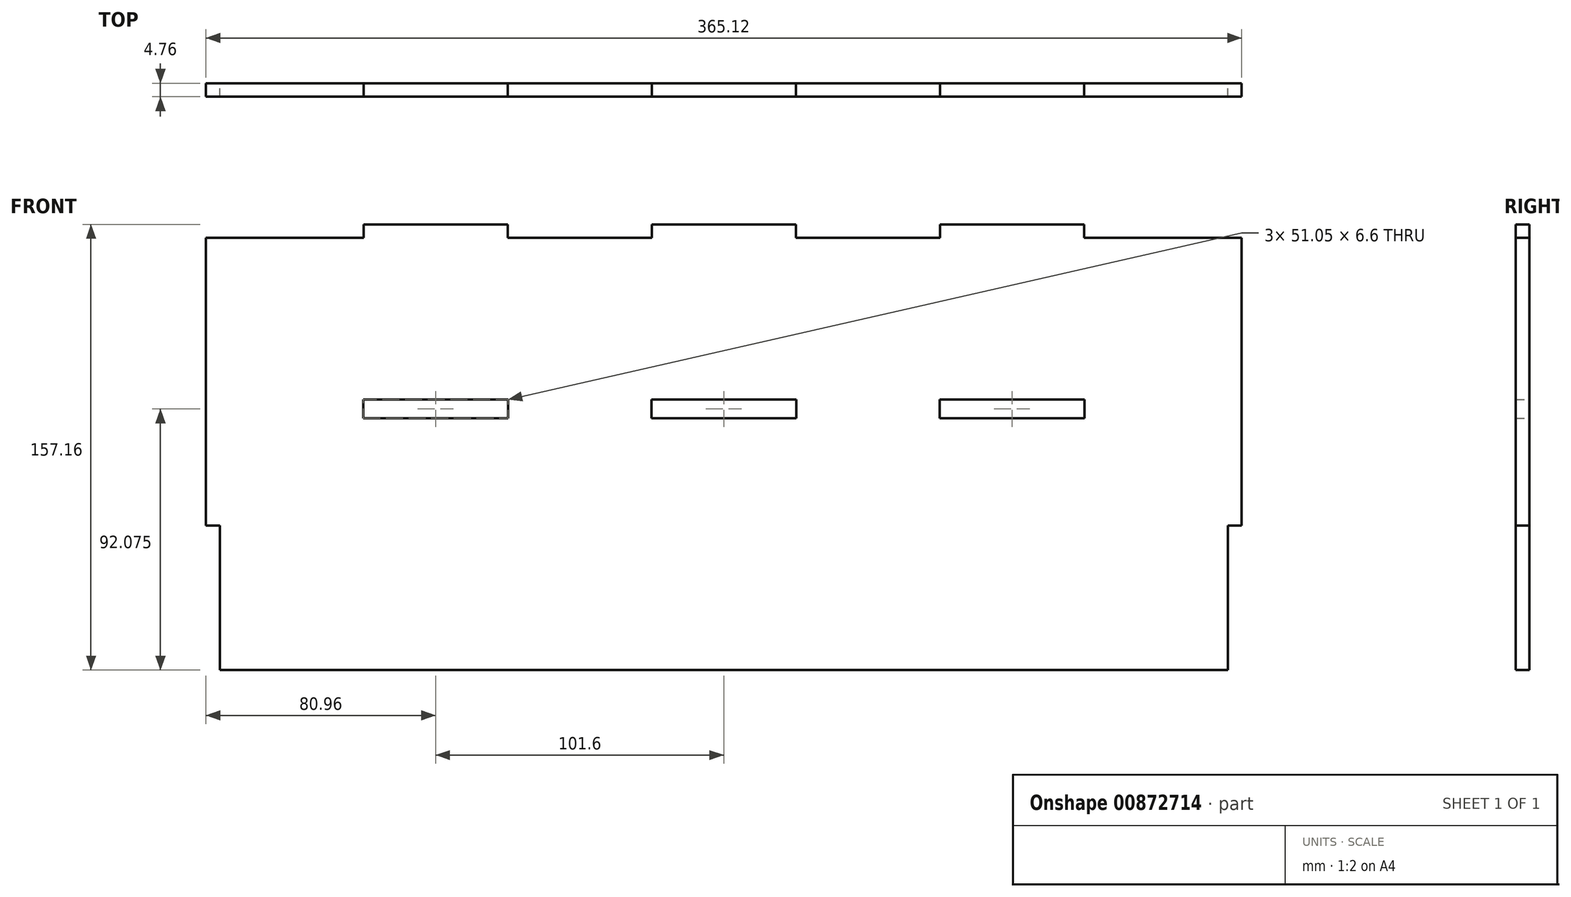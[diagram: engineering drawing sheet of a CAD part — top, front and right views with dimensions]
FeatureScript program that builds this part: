
annotation { "Feature Type Name" : "Feature", "Feature Type Description" : "" }
export const myFeature = defineFeature(function(context is Context, id is Id, definition is map)
    precondition{}
    {
        {
            var Q0;
            Q0=qCreatedBy(makeId("Front.planeOp"),FACE);
            var sketch = newSketch(context, id + "F0", { "sketchPlane" : qUnion([Q0])});
            skLineSegment(sketch, "E0.bottom", {"start": v(-182.56, 76.2) * mm, "end": v(182.56, 76.2) * mm});
            skLineSegment(sketch, "E0.top", {"start": v(-182.56, -76.2) * mm, "end": v(182.56, -76.2) * mm});
            skLineSegment(sketch, "E0.left", {"start": v(-182.56, 76.2) * mm, "end": v(-182.56, -76.2) * mm});
            skLineSegment(sketch, "E0.right", {"start": v(182.56, 76.2) * mm, "end": v(182.56, -76.2) * mm});
            skPoint(sketch, "E0.middle", {"position": v(0, 0) * mm});
            skLineSegment(sketch, "E1.0", {"start": v(-177.8, 76.2) * mm, "end": v(-177.8, -76.2) * mm, "construction": true});
            skLineSegment(sketch, "E2.0", {"start": v(177.8, 76.2) * mm, "end": v(177.8, -76.2) * mm, "construction": true});
            skLineSegment(sketch, "E3.bottom", {"start": v(-127, 19.05) * mm, "end": v(-76.2, 19.05) * mm});
            skLineSegment(sketch, "E3.top", {"start": v(-127, 12.7) * mm, "end": v(-76.2, 12.7) * mm});
            skLineSegment(sketch, "E3.left", {"start": v(-127, 19.05) * mm, "end": v(-127, 12.7) * mm});
            skLineSegment(sketch, "E3.right", {"start": v(-76.2, 19.05) * mm, "end": v(-76.2, 12.7) * mm});
            skLineSegment(sketch, "E4.0", {"start": v(-127.13, 19.18) * mm, "end": v(-76.07, 19.18) * mm});
            skLineSegment(sketch, "E4.1", {"start": v(-127.13, 19.18) * mm, "end": v(-127.13, 12.57) * mm});
            skLineSegment(sketch, "E4.2", {"start": v(-127.13, 12.57) * mm, "end": v(-76.07, 12.57) * mm});
            skLineSegment(sketch, "E4.3", {"start": v(-76.07, 19.18) * mm, "end": v(-76.07, 12.57) * mm});
            skLineSegment(sketch, "E5.1.0.0", {"start": v(-25.53, 19.18) * mm, "end": v(-25.53, 12.57) * mm});
            skLineSegment(sketch, "E5.1.0.1", {"start": v(-25.53, 19.18) * mm, "end": v(25.53, 19.18) * mm});
            skLineSegment(sketch, "E5.1.0.2", {"start": v(-25.53, 12.57) * mm, "end": v(25.53, 12.57) * mm});
            skLineSegment(sketch, "E5.1.0.3", {"start": v(25.4, 19.05) * mm, "end": v(25.4, 12.7) * mm});
            skLineSegment(sketch, "E5.1.0.4", {"start": v(-25.4, 19.05) * mm, "end": v(25.4, 19.05) * mm});
            skLineSegment(sketch, "E5.1.0.5", {"start": v(25.53, 19.18) * mm, "end": v(25.53, 12.57) * mm});
            skLineSegment(sketch, "E5.1.0.6", {"start": v(-25.4, 19.05) * mm, "end": v(-25.4, 12.7) * mm});
            skLineSegment(sketch, "E5.1.0.7", {"start": v(-25.4, 12.7) * mm, "end": v(25.4, 12.7) * mm});
            skLineSegment(sketch, "E5.2.0.0", {"start": v(76.07, 19.18) * mm, "end": v(76.07, 12.57) * mm});
            skLineSegment(sketch, "E5.2.0.1", {"start": v(76.07, 19.18) * mm, "end": v(127.13, 19.18) * mm});
            skLineSegment(sketch, "E5.2.0.2", {"start": v(76.07, 12.57) * mm, "end": v(127.13, 12.57) * mm});
            skLineSegment(sketch, "E5.2.0.3", {"start": v(127, 19.05) * mm, "end": v(127, 12.7) * mm});
            skLineSegment(sketch, "E5.2.0.4", {"start": v(76.2, 19.05) * mm, "end": v(127, 19.05) * mm});
            skLineSegment(sketch, "E5.2.0.5", {"start": v(127.13, 19.18) * mm, "end": v(127.13, 12.57) * mm});
            skLineSegment(sketch, "E5.2.0.6", {"start": v(76.2, 19.05) * mm, "end": v(76.2, 12.7) * mm});
            skLineSegment(sketch, "E5.2.0.7", {"start": v(76.2, 12.7) * mm, "end": v(127, 12.7) * mm});
            skLineSegment(sketch, "E5.direction1", {"start": v(-127, 12.7) * mm, "end": v(-25.4, 12.7) * mm, "construction": true});
            skLineSegment(sketch, "E6.bottom", {"start": v(-182.56, -76.2) * mm, "end": v(-177.8, -76.2) * mm});
            skLineSegment(sketch, "E6.top", {"start": v(-182.56, -25.4) * mm, "end": v(-177.8, -25.4) * mm});
            skLineSegment(sketch, "E6.left", {"start": v(-182.56, -76.2) * mm, "end": v(-182.56, -25.4) * mm});
            skLineSegment(sketch, "E6.right", {"start": v(-177.8, -76.2) * mm, "end": v(-177.8, -25.4) * mm});
            skLineSegment(sketch, "E7", {"start": v(0, 76.2) * mm, "end": v(0, -76.2) * mm, "construction": true});
            skLineSegment(sketch, "E8.MirrorCS", {"start": v(182.56, -76.2) * mm, "end": v(177.8, -76.2) * mm});
            skLineSegment(sketch, "E9.MirrorCS", {"start": v(182.56, -25.4) * mm, "end": v(177.8, -25.4) * mm});
            skLineSegment(sketch, "E10.MirrorCS", {"start": v(182.56, -76.2) * mm, "end": v(182.56, -25.4) * mm});
            skLineSegment(sketch, "E11.MirrorCS", {"start": v(177.8, -76.2) * mm, "end": v(177.8, -25.4) * mm});
            skLineSegment(sketch, "E12.0", {"start": v(-182.69, -76.33) * mm, "end": v(-177.67, -76.33) * mm});
            skLineSegment(sketch, "E12.1", {"start": v(-182.69, -76.33) * mm, "end": v(-182.69, -25.27) * mm});
            skLineSegment(sketch, "E12.2", {"start": v(-182.69, -25.27) * mm, "end": v(-177.67, -25.27) * mm});
            skLineSegment(sketch, "E12.3", {"start": v(-177.67, -76.33) * mm, "end": v(-177.67, -25.27) * mm});
            skLineSegment(sketch, "E13.bottom", {"start": v(-127, 76.2) * mm, "end": v(-76.2, 76.2) * mm});
            skLineSegment(sketch, "E13.top", {"start": v(-127, 80.96) * mm, "end": v(-76.2, 80.96) * mm});
            skLineSegment(sketch, "E13.left", {"start": v(-127, 76.2) * mm, "end": v(-127, 80.96) * mm});
            skLineSegment(sketch, "E13.right", {"start": v(-76.2, 76.2) * mm, "end": v(-76.2, 80.96) * mm});
            skLineSegment(sketch, "E14.1.0.0", {"start": v(-25.4, 80.96) * mm, "end": v(25.4, 80.96) * mm});
            skLineSegment(sketch, "E14.1.0.1", {"start": v(-25.4, 76.2) * mm, "end": v(25.4, 76.2) * mm});
            skLineSegment(sketch, "E14.1.0.2", {"start": v(-25.4, 76.2) * mm, "end": v(-25.4, 80.96) * mm});
            skLineSegment(sketch, "E14.1.0.3", {"start": v(25.4, 76.2) * mm, "end": v(25.4, 80.96) * mm});
            skLineSegment(sketch, "E14.2.0.0", {"start": v(76.2, 80.96) * mm, "end": v(127, 80.96) * mm});
            skLineSegment(sketch, "E14.2.0.1", {"start": v(76.2, 76.2) * mm, "end": v(127, 76.2) * mm});
            skLineSegment(sketch, "E14.2.0.2", {"start": v(76.2, 76.2) * mm, "end": v(76.2, 80.96) * mm});
            skLineSegment(sketch, "E14.2.0.3", {"start": v(127, 76.2) * mm, "end": v(127, 80.96) * mm});
            skLineSegment(sketch, "E14.direction1", {"start": v(-127, 76.2) * mm, "end": v(-25.4, 76.2) * mm, "construction": true});
            skLineSegment(sketch, "E15.MirrorCS", {"start": v(182.69, -76.33) * mm, "end": v(177.67, -76.33) * mm});
            skLineSegment(sketch, "E16.MirrorCS", {"start": v(182.69, -25.27) * mm, "end": v(177.67, -25.27) * mm});
            skLineSegment(sketch, "E17.MirrorCS", {"start": v(182.69, -76.33) * mm, "end": v(182.69, -25.27) * mm});
            skLineSegment(sketch, "E18.MirrorCS", {"start": v(177.67, -76.33) * mm, "end": v(177.67, -25.27) * mm});
            skSolve(sketch);
        }
        {
            var Q0;
            Q0=makeQuery(id+"F0.imprint","IMPRINT",FACE,{"disambiguationData":[TD([[makeQuery(id+"F0.imprint","IMPRINT",EDGE,{"derivedFrom":sQuery(id+"F0.wireOp",EDGE,"E4.0")}),1.0]])]});
            var Q1;
            Q1=makeQuery(id+"F0.imprint","IMPRINT",FACE,{"disambiguationData":[TD([[makeQuery(id+"F0.imprint","IMPRINT",EDGE,{"derivedFrom":sQuery(id+"F0.wireOp",EDGE,"E13.top")}),-1.0]])]});
            var Q2;
            Q2=makeQuery(id+"F0.imprint","IMPRINT",FACE,{"disambiguationData":[TD([[makeQuery(id+"F0.imprint","IMPRINT",EDGE,{"derivedFrom":sQuery(id+"F0.wireOp",EDGE,"E14.1.0.0")}),-1.0]])]});
            var Q3;
            Q3=makeQuery(id+"F0.imprint","IMPRINT",FACE,{"disambiguationData":[TD([[makeQuery(id+"F0.imprint","IMPRINT",EDGE,{"derivedFrom":sQuery(id+"F0.wireOp",EDGE,"E14.2.0.0")}),-1.0]])]});
            extrude(context, id + "F1", {"entities" : qUnion([Q0, Q1, Q2, Q3]), "depth" : 4.76 * mm, "offsetDistance" : 25.4 * mm});
        }
    });
